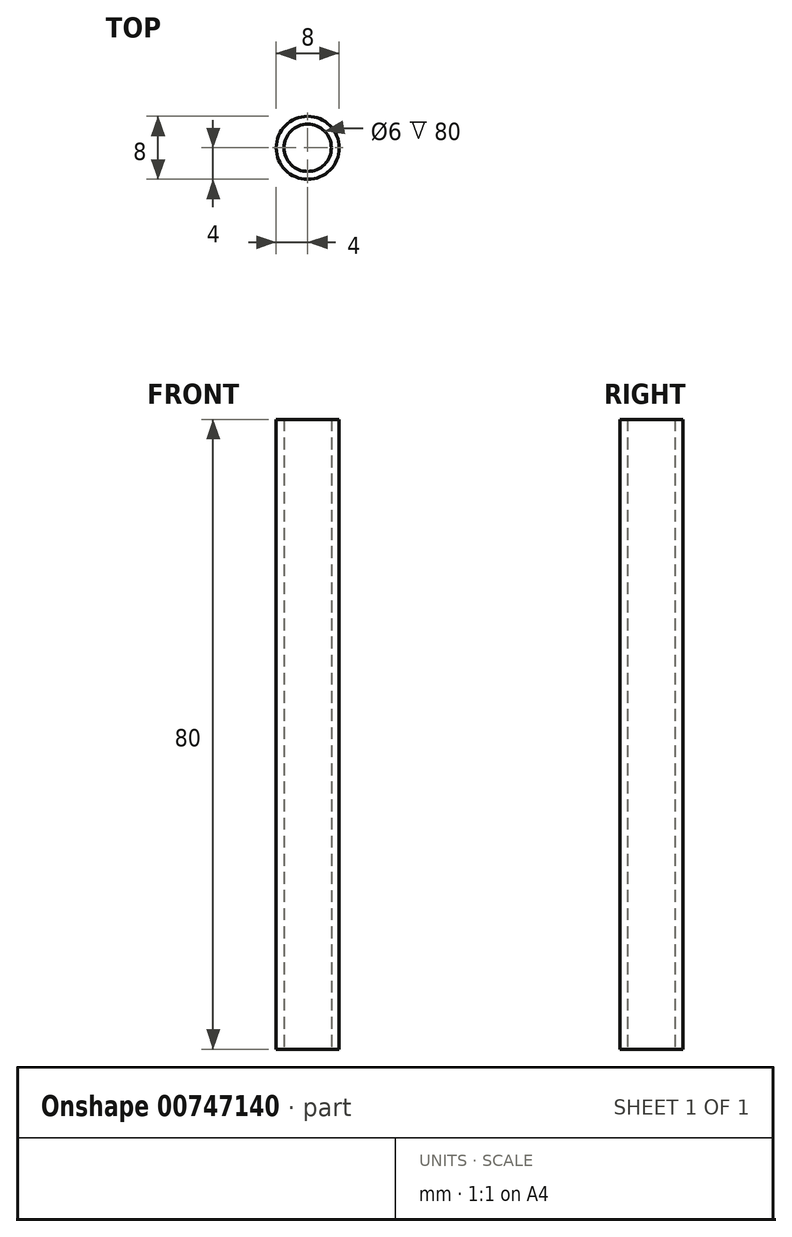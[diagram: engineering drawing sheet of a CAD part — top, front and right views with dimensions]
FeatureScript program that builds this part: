
annotation { "Feature Type Name" : "Feature", "Feature Type Description" : "" }
export const myFeature = defineFeature(function(context is Context, id is Id, definition is map)
    precondition{}
    {
        {
            var Q0;
            Q0=qCreatedBy(makeId("Top.planeOp"),FACE);
            var sketch = newSketch(context, id + "F0", { "sketchPlane" : qUnion([Q0])});
            skCircle(sketch, "E0", {"center": v(0, 0) * mm, "radius": 4 * mm});
            skCircle(sketch, "E1.0", {"center": v(0, 0) * mm, "radius": 3 * mm});
            skSolve(sketch);
        }
        {
            var Q0;
            Q0=makeQuery(id+"F0.imprint","IMPRINT",FACE,{"disambiguationData":[TD([[makeQuery(id+"F0.imprint","IMPRINT",EDGE,{"derivedFrom":sQuery(id+"F0.wireOp",EDGE,"E0")}),1.0]])]});
            extrude(context, id + "F1", {"entities" : qUnion([Q0]), "depth" : 80 * mm, "offsetDistance" : 25 * mm});
        }
    });
